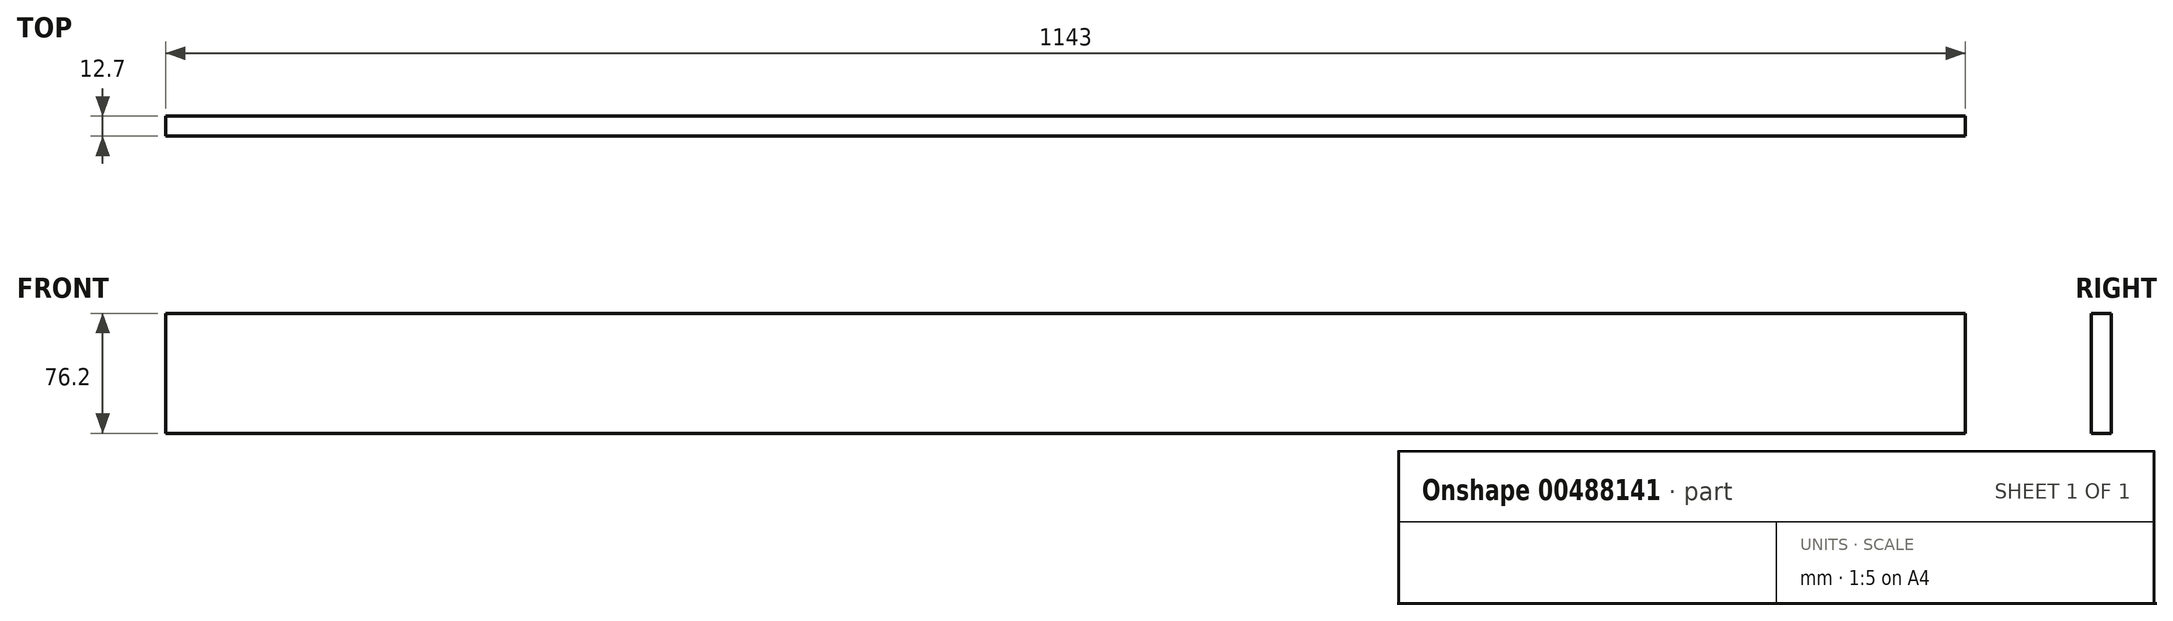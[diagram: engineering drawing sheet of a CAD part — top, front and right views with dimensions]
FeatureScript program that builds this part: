
annotation { "Feature Type Name" : "Feature", "Feature Type Description" : "" }
export const myFeature = defineFeature(function(context is Context, id is Id, definition is map)
    precondition{}
    {
        {
            var Q0;
            Q0=qCreatedBy(makeId("Front.planeOp"),FACE);
            var sketch = newSketch(context, id + "F0", { "sketchPlane" : qUnion([Q0])});
            skLineSegment(sketch, "E0", {"start": v(0, 0) * mm, "end": v(0, 76.2) * mm});
            skLineSegment(sketch, "E1", {"start": v(0, 76.2) * mm, "end": v(1143, 76.2) * mm});
            skLineSegment(sketch, "E2", {"start": v(1143, 76.2) * mm, "end": v(1143, 0) * mm});
            skLineSegment(sketch, "E3", {"start": v(1143, 0) * mm, "end": v(0, 0) * mm});
            skSolve(sketch);
        }
        {
            var Q0;
            Q0=makeQuery(id+"F0.imprint","IMPRINT",FACE,{"disambiguationData":[TD([[makeQuery(id+"F0.imprint","IMPRINT",EDGE,{"derivedFrom":sQuery(id+"F0.wireOp",EDGE,"E0")}),-1.0]])]});
            extrude(context, id + "F1", {"entities" : qUnion([Q0]), "depth" : 12.7 * mm, "offsetDistance" : 25.4 * mm});
        }
    });
